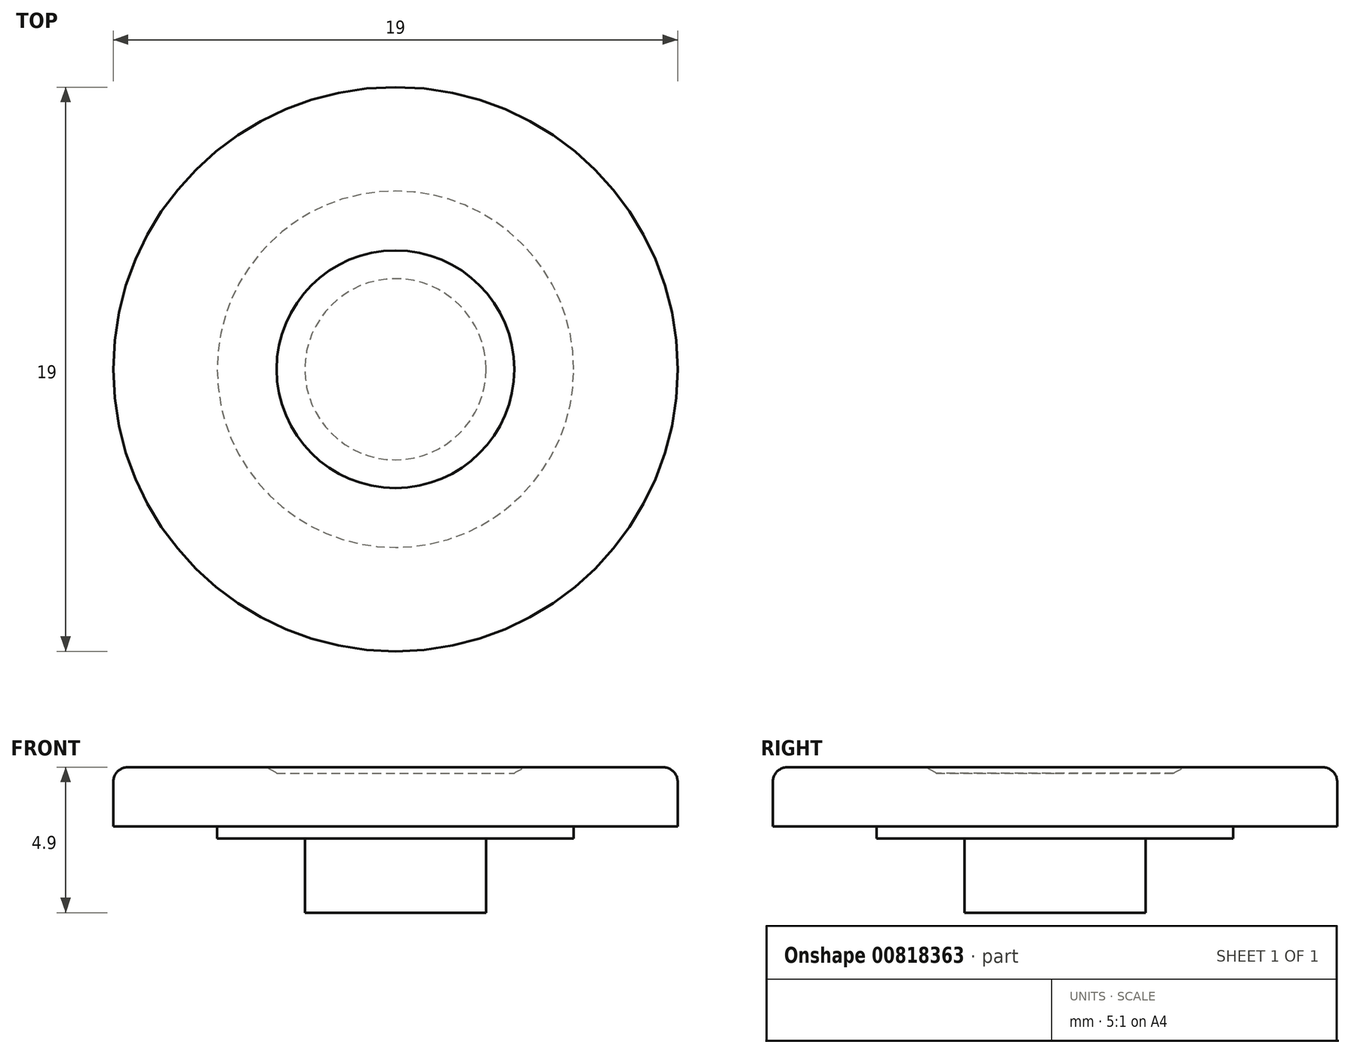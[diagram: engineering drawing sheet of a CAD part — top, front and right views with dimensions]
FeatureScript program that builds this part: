
annotation { "Feature Type Name" : "Feature", "Feature Type Description" : "" }
export const myFeature = defineFeature(function(context is Context, id is Id, definition is map)
    precondition{}
    {
        {
            var Q0;
            Q0=qCreatedBy(makeId("Front.planeOp"),FACE);
            var sketch = newSketch(context, id + "F0", { "sketchPlane" : qUnion([Q0])});
            skLineSegment(sketch, "E0", {"start": v(0, 0) * mm, "end": v(9.5, 0) * mm});
            skPoint(sketch, "E1.snap10", {"position": v(4.75, 0) * mm});
            skLineSegment(sketch, "E2.bottom", {"start": v(0, 0) * mm, "end": v(3.05, 0) * mm});
            skLineSegment(sketch, "E2.top", {"start": v(0, -2.9) * mm, "end": v(3.05, -2.9) * mm});
            skLineSegment(sketch, "E2.left", {"start": v(0, 0) * mm, "end": v(0, -2.9) * mm});
            skLineSegment(sketch, "E2.right", {"start": v(3.05, 0) * mm, "end": v(3.05, -2.9) * mm});
            skLineSegment(sketch, "E3.bottom", {"start": v(0, 0) * mm, "end": v(6, 0) * mm});
            skLineSegment(sketch, "E3.top", {"start": v(0, -0.4) * mm, "end": v(6, -0.4) * mm});
            skLineSegment(sketch, "E3.left", {"start": v(0, 0) * mm, "end": v(0, -0.4) * mm});
            skLineSegment(sketch, "E3.right", {"start": v(6, 0) * mm, "end": v(6, -0.4) * mm});
            skPoint(sketch, "E4", {"position": v(3.05, -0.4) * mm});
            skLineSegment(sketch, "E5", {"start": v(0, 0) * mm, "end": v(0, 1.8) * mm});
            skLineSegment(sketch, "E6", {"start": v(0, 1.8) * mm, "end": v(4, 1.8) * mm});
            skLineSegment(sketch, "E7", {"start": v(4, 1.8) * mm, "end": v(4, 2) * mm});
            skLineSegment(sketch, "E8", {"start": v(4, 2) * mm, "end": v(9.5, 2) * mm});
            skLineSegment(sketch, "E9", {"start": v(9.5, 2) * mm, "end": v(9.5, 0) * mm});
            skSolve(sketch);
        }
        {
            var Q0;
            Q0=qSketchRegion(id+"F0",true);
            var Q1;
            Q1=sQuery(id+"F0.wireOp",EDGE,"E5");
            revolve(context, id + "F1", {"surfaceOperationType" : NewSurfaceOperationType.NEW, "entities" : qUnion([Q0]), "axis" : qUnion([Q1]), "revolveType" : RevolveType.FULL});
        }
        {
            var Q0;
            Q0=makeQuery(id+"F1.opRevolve","SWEPT_EDGE",EDGE,{"disambiguationData":[OSD([sQuery(id+"F0.wireOp",EDGE,"9hwaFN4s-kBqj-5SZZ-FVYH-1m46pSyMPwgE"),sQuery(id+"F0.wireOp",EDGE,"w00q5z8J-IB3I-pAUQ-ONzX-yISjesTEle08")])]});
            var Q1;
            Q1=makeQuery(id+"F1.opRevolve","SWEPT_EDGE",EDGE,{"disambiguationData":[OSD([sQuery(id+"F0.wireOp",EDGE,"E8"),sQuery(id+"F0.wireOp",EDGE,"E9")])]});
            fillet(context, id + "F2", {"entities" : qUnion([Q0, Q1]), "radius" : 0.5 * mm, "tangentPropagation" : true, "allowEdgeOverflow" : false});
        }
        {
            var Q0;
            Q0=makeQuery(id+"F1.opRevolve","SWEPT_EDGE",EDGE,{"disambiguationData":[OSD([sQuery(id+"F0.wireOp",EDGE,"ev8LMBu1-Yj06-iMLD-In9u-e10gH1f179TZ"),sQuery(id+"F0.wireOp",EDGE,"w00q5z8J-IB3I-pAUQ-ONzX-yISjesTEle08")])]});
            var Q1;
            Q1=makeQuery(id+"F1.opRevolve","SWEPT_EDGE",EDGE,{"disambiguationData":[OSD([sQuery(id+"F0.wireOp",EDGE,"E7"),sQuery(id+"F0.wireOp",EDGE,"E8")])]});
            fillet(context, id + "F3", {"entities" : qUnion([Q0, Q1]), "radius" : 1 * mm, "tangentPropagation" : true, "allowEdgeOverflow" : false});
        }
    });
